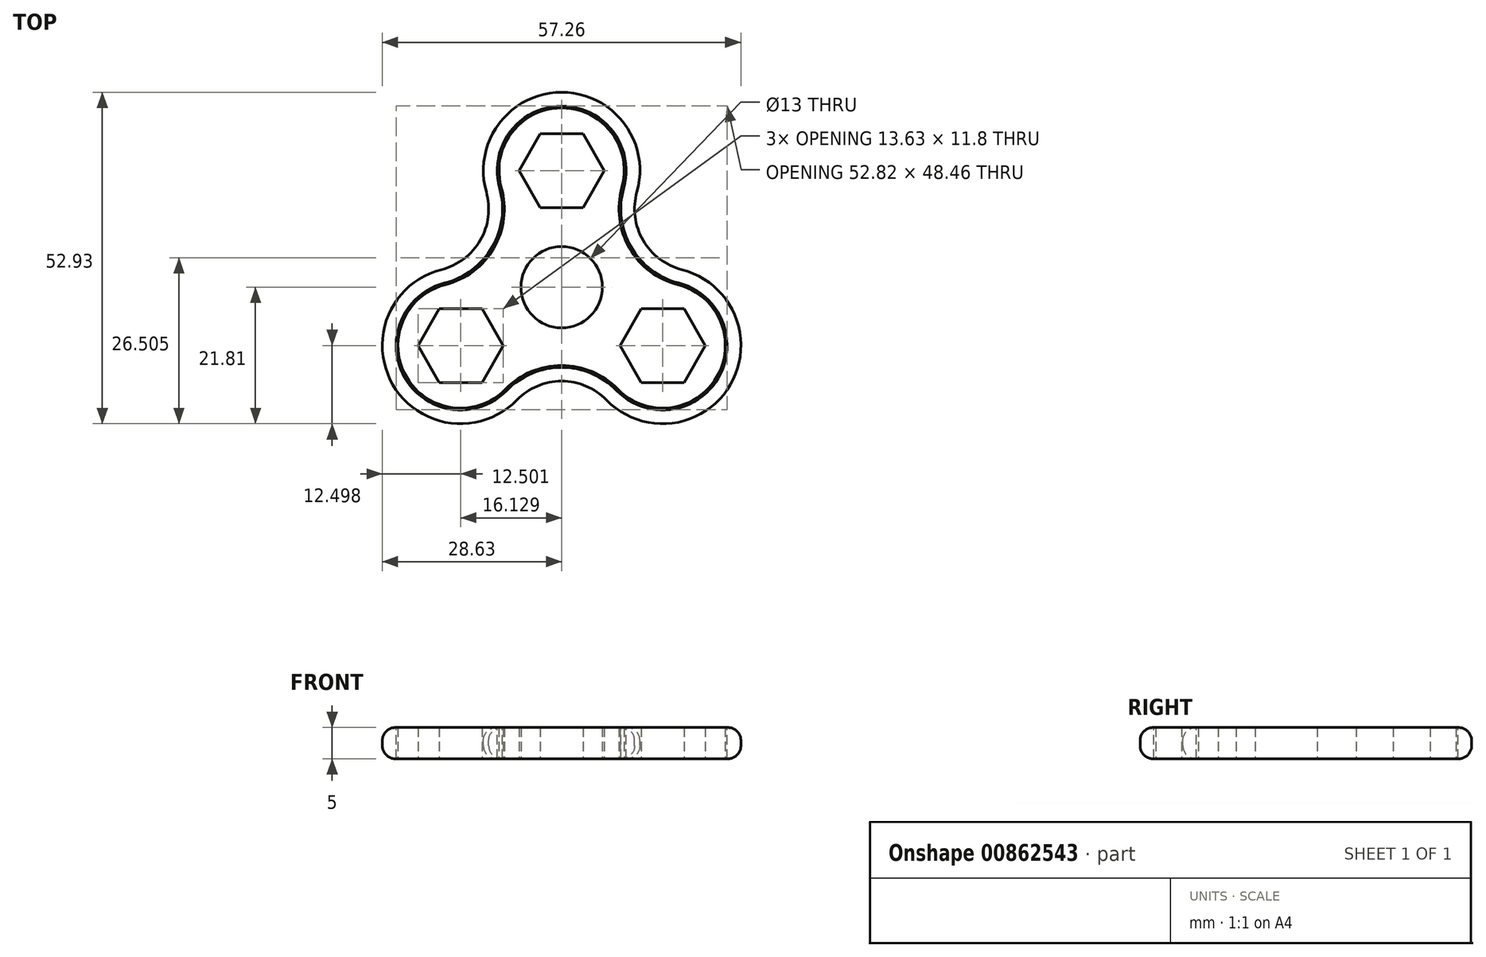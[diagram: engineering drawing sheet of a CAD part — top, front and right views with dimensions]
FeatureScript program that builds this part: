
annotation { "Feature Type Name" : "Feature", "Feature Type Description" : "" }
export const myFeature = defineFeature(function(context is Context, id is Id, definition is map)
    precondition{}
    {
        {
            var Q0;
            Q0=qCreatedBy(makeId("Top.planeOp"),FACE);
            var sketch = newSketch(context, id + "F0", { "sketchPlane" : qUnion([Q0])});
            skCircle(sketch, "E0", {"center": v(0, 0) * mm, "radius": 6.5 * mm});
            skCircle(sketch, "E1.cCircle", {"center": v(0, 0) * mm, "radius": 12.5 * mm, "construction": true});
            skLineSegment(sketch, "E1.0", {"start": v(-7.22, 12.5) * mm, "end": v(7.22, 12.5) * mm});
            skLineSegment(sketch, "E1.1", {"start": v(7.22, 12.5) * mm, "end": v(14.43, 0) * mm});
            skLineSegment(sketch, "E1.2", {"start": v(14.43, 0) * mm, "end": v(7.22, -12.5) * mm});
            skLineSegment(sketch, "E1.3", {"start": v(7.22, -12.5) * mm, "end": v(-7.22, -12.5) * mm});
            skLineSegment(sketch, "E1.4", {"start": v(-7.22, -12.5) * mm, "end": v(-14.43, 0) * mm});
            skLineSegment(sketch, "E1.5", {"start": v(-14.43, 0) * mm, "end": v(-7.22, 12.5) * mm});
            skPoint(sketch, "E1.0.midPoint", {"position": v(0, 12.5) * mm});
            skCircle(sketch, "E2.cCircle", {"center": v(0, 18.62) * mm, "radius": 10 * mm});
            skLineSegment(sketch, "E2.0", {"start": v(-5.77, 28.62) * mm, "end": v(5.77, 28.62) * mm});
            skLineSegment(sketch, "E2.1", {"start": v(5.77, 28.62) * mm, "end": v(11.55, 18.62) * mm, "construction": true});
            skLineSegment(sketch, "E2.2", {"start": v(11.55, 18.62) * mm, "end": v(5.77, 8.62) * mm, "construction": true});
            skLineSegment(sketch, "E2.3", {"start": v(5.77, 8.62) * mm, "end": v(-5.77, 8.62) * mm});
            skLineSegment(sketch, "E2.4", {"start": v(-5.77, 8.62) * mm, "end": v(-11.55, 18.62) * mm, "construction": true});
            skLineSegment(sketch, "E2.5", {"start": v(-11.55, 18.62) * mm, "end": v(-5.77, 28.62) * mm, "construction": true});
            skPoint(sketch, "E2.0.midPoint", {"position": v(0, 28.62) * mm});
            skCircle(sketch, "E3.cCircle", {"center": v(0, 18.62) * mm, "radius": 5.9 * mm, "construction": true});
            skLineSegment(sketch, "E3.0", {"start": v(-3.4, 24.52) * mm, "end": v(3.4, 24.52) * mm});
            skLineSegment(sketch, "E3.1", {"start": v(3.4, 24.52) * mm, "end": v(6.81, 18.62) * mm});
            skLineSegment(sketch, "E3.2", {"start": v(6.81, 18.62) * mm, "end": v(3.4, 12.72) * mm});
            skLineSegment(sketch, "E3.3", {"start": v(3.4, 12.72) * mm, "end": v(-3.4, 12.72) * mm});
            skLineSegment(sketch, "E3.4", {"start": v(-3.4, 12.72) * mm, "end": v(-6.81, 18.62) * mm});
            skLineSegment(sketch, "E3.5", {"start": v(-6.81, 18.62) * mm, "end": v(-3.4, 24.52) * mm});
            skPoint(sketch, "E3.0.midPoint", {"position": v(0, 24.52) * mm});
            skCircle(sketch, "E4", {"center": v(21.65, 12.5) * mm, "radius": 12.5 * mm});
            skLineSegment(sketch, "E5", {"start": v(0, 8.62) * mm, "end": v(0, 12.5) * mm, "construction": true});
            skCircle(sketch, "E6.MirrorC", {"center": v(-21.65, 12.5) * mm, "radius": 12.5 * mm});
            skLineSegment(sketch, "E7", {"start": v(14.43, 0) * mm, "end": v(26.22, 0) * mm, "construction": true});
            skSolve(sketch);
        }
        {
            var Q0;
            Q0=makeQuery(id+"F0.imprint","IMPRINT",FACE,{"disambiguationData":[TD([[makeQuery(id+"F0.imprint","IMPRINT",EDGE,{"derivedFrom":sQuery(id+"F0.wireOp",EDGE,"E0")}),-1.0]])]});
            var Q1;
            {var subQ1=sQuery(id+"F0.wireOp",EDGE,"E1.0");Q1=makeQuery(id+"F0.imprint","IMPRINT",FACE,{"disambiguationData":[TD([[makeQuery(id+"F0.imprint","IMPRINT",EDGE,{"derivedFrom":subQ1}),-1.0]])]});}
            extrude(context, id + "F1", {"entities" : qUnion([Q0, Q1]), "depth" : 5 * mm, "offsetDistance" : 25 * mm});
        }
        {
            var Q0;
            {var subQ5=sQuery(id+"F0.wireOp",EDGE,"E1.0");Q0=makeQuery(id+"F0.imprint","IMPRINT",FACE,{"disambiguationData":[TD([[makeQuery(id+"F0.imprint","IMPRINT",EDGE,{"derivedFrom":subQ5}),1.0]])]});}
            var Q1;
            {var subQ1=sQuery(id+"F0.wireOp",EDGE,"E1.0");Q1=makeQuery(id+"F0.imprint","IMPRINT",FACE,{"disambiguationData":[TD([[makeQuery(id+"F0.imprint","IMPRINT",EDGE,{"derivedFrom":subQ1}),-1.0]])]});}
            var Q2;
            {var subQ0=sQuery(id+"F0.wireOp",EDGE,"E6.MirrorC");var subQ1=sQuery(id+"F0.wireOp",EDGE,"E1.5");var subQ2=makeQuery(id+"F0.imprint","INTERSECT",VERTEX,{"derivedFrom":[subQ1,subQ0]});Q2=makeQuery(id+"F0.imprint","IMPRINT",FACE,{"disambiguationData":[TD([[makeQuery(id+"F0.imprint","IMPRINT",EDGE,{"disambiguationData":[TD([[subQ2,-1.0]])],"derivedFrom":subQ1}),1.0]])]});}
            var Q3;
            {var subQ0=sQuery(id+"F0.wireOp",EDGE,"E4");var subQ1=sQuery(id+"F0.wireOp",EDGE,"E1.1");var subQ2=makeQuery(id+"F0.imprint","INTERSECT",VERTEX,{"derivedFrom":[subQ1,subQ0]});Q3=makeQuery(id+"F0.imprint","IMPRINT",FACE,{"disambiguationData":[TD([[makeQuery(id+"F0.imprint","IMPRINT",EDGE,{"disambiguationData":[TD([[subQ2,1.0]])],"derivedFrom":subQ1}),1.0]])]});}
            extrude(context, id + "F2", {"entities" : qUnion([Q0, Q1, Q2, Q3]), "depth" : 5 * mm, "offsetDistance" : 25 * mm});
        }
        {
            var Q0;
            Q0=makeQuery(id+"F2.opExtrude","SWEPT_BODY",BODY,{"disambiguationData":[OSD([sQuery(id+"F0.wireOp",EDGE,"E2.0"),sQuery(id+"F0.wireOp",EDGE,"E2.1"),sQuery(id+"F0.wireOp",EDGE,"E2.2"),sQuery(id+"F0.wireOp",EDGE,"E2.3"),sQuery(id+"F0.wireOp",EDGE,"E2.4"),sQuery(id+"F0.wireOp",EDGE,"E2.5"),sQuery(id+"F0.wireOp",EDGE,"E3.0"),sQuery(id+"F0.wireOp",EDGE,"E3.1"),sQuery(id+"F0.wireOp",EDGE,"E3.2"),sQuery(id+"F0.wireOp",EDGE,"E3.3"),sQuery(id+"F0.wireOp",EDGE,"E3.4"),sQuery(id+"F0.wireOp",EDGE,"E3.5")])]});
            var Q1;
            Q1=sQuery(id+"F0.wireOp",EDGE,"E1.cCircle");
            circularPattern(context, id + "F3", {"operationType" : NewBodyOperationType.ADD, "entities" : qUnion([Q0]), "axis" : qUnion([Q1]), "angle" : 360 * degree, "instanceCount" : 3, "equalSpace" : true});
        }
        {
            var Q0;
            {var subQ0=sQuery(id+"F0.wireOp",EDGE,"E2.cCircle");var subQ1=sQuery(id+"F0.wireOp",EDGE,"E1.5");var subQ2=sQuery(id+"F0.wireOp",EDGE,"E1.1");var subQ3=makeQuery(id+"F2.opExtrude","CAP_FACE",FACE,{"disambiguationData":[OSD([subQ2,subQ1,subQ0,sQuery(id+"F0.wireOp",EDGE,"E3.0"),sQuery(id+"F0.wireOp",EDGE,"E3.1"),sQuery(id+"F0.wireOp",EDGE,"E3.2"),sQuery(id+"F0.wireOp",EDGE,"E3.3"),sQuery(id+"F0.wireOp",EDGE,"E3.4"),sQuery(id+"F0.wireOp",EDGE,"E3.5"),sQuery(id+"F0.wireOp",EDGE,"E4"),sQuery(id+"F0.wireOp",EDGE,"E6.MirrorC")])],"isStart":false});Q0=makeQuery(id+"F3.boolean.opBoolean","MERGE",FACE,{"derivedFrom":[makeQuery(id+"F1.opExtrude","CAP_FACE",FACE,{"disambiguationData":[OSD([sQuery(id+"F0.wireOp",EDGE,"E0"),subQ2,sQuery(id+"F0.wireOp",EDGE,"E1.2"),sQuery(id+"F0.wireOp",EDGE,"E1.3"),sQuery(id+"F0.wireOp",EDGE,"E1.4"),subQ1,subQ0])],"isStart":false}),subQ3,makeQuery(id+"F3.opPattern","COPY",FACE,{"derivedFrom":subQ3,"instanceName":"1"}),makeQuery(id+"F3.opPattern","COPY",FACE,{"derivedFrom":subQ3,"instanceName":"2"})]});}
            var sketch = newSketch(context, id + "F4", { "sketchPlane" : qUnion([Q0])});
            skArc(sketch, "E8.0", {"start": v(7.17, -18.03) * mm, "mid": v(26.95, -15.56) * mm, "end": v(19.2, 2.8) * mm});
            skArc(sketch, "E8.1", {"start": v(12.03, 15.22) * mm, "mid": v(0, 31.12) * mm, "end": v(-12.03, 15.22) * mm});
            skArc(sketch, "E8.2", {"start": v(-12.03, 15.22) * mm, "mid": v(-13, 7.5) * mm, "end": v(-19.2, 2.8) * mm});
            skArc(sketch, "E8.3", {"start": v(19.2, 2.8) * mm, "mid": v(13, 7.5) * mm, "end": v(12.03, 15.22) * mm});
            skArc(sketch, "E8.4", {"start": v(-19.2, 2.8) * mm, "mid": v(-26.95, -15.56) * mm, "end": v(-7.17, -18.03) * mm});
            skArc(sketch, "E8.5", {"start": v(-7.17, -18.03) * mm, "mid": v(0, -15) * mm, "end": v(7.17, -18.03) * mm});
            skArc(sketch, "E9.0", {"start": v(8.75, -16.5) * mm, "mid": v(25.05, -14.46) * mm, "end": v(18.66, 0.67) * mm});
            skArc(sketch, "E9.1", {"start": v(9.91, 15.82) * mm, "mid": v(0, 28.92) * mm, "end": v(-9.91, 15.82) * mm});
            skArc(sketch, "E9.2", {"start": v(-9.91, 15.82) * mm, "mid": v(-11.09, 6.4) * mm, "end": v(-18.66, 0.67) * mm});
            skArc(sketch, "E9.3", {"start": v(18.66, 0.67) * mm, "mid": v(11.09, 6.4) * mm, "end": v(9.91, 15.82) * mm});
            skArc(sketch, "E9.4", {"start": v(-18.66, 0.67) * mm, "mid": v(-25.05, -14.46) * mm, "end": v(-8.75, -16.5) * mm});
            skArc(sketch, "E9.5", {"start": v(-8.75, -16.5) * mm, "mid": v(0, -12.8) * mm, "end": v(8.75, -16.5) * mm});
            skSolve(sketch);
        }
        {
            var Q0;
            Q0=makeQuery(id+"F4.imprint","IMPRINT",FACE,{"disambiguationData":[TD([[makeQuery(id+"F4.imprint","IMPRINT",EDGE,{"derivedFrom":sQuery(id+"F4.wireOp",EDGE,"E8.0")}),1.0]])]});
            extrude(context, id + "F5", {"entities" : qUnion([Q0]), "oppositeDirection" : true, "depth" : 5 * mm, "offsetDistance" : 25 * mm});
        }
        {
            var Q0;
            Q0=makeQuery(id+"F5.opExtrude","CAP_EDGE",EDGE,{"disambiguationData":[OSD([sQuery(id+"F4.wireOp",EDGE,"E8.4")])],"isStart":true});
            var Q1;
            Q1=makeQuery(id+"F5.opExtrude","CAP_EDGE",EDGE,{"disambiguationData":[OSD([sQuery(id+"F4.wireOp",EDGE,"E8.4")])],"isStart":false});
            fillet(context, id + "F6", {"entities" : qUnion([Q0, Q1]), "radius" : 2.1 * mm, "tangentPropagation" : true, "allowEdgeOverflow" : false});
        }
    });
